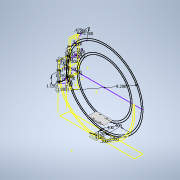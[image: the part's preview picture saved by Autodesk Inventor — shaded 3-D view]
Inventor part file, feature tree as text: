
AUTODESK INVENTOR PART (.ipt)
format: ipt  version: 2022 (Build 260153000, 153)  size: 395,776 bytes
history: native  units: in
note: dims shown in document units (in); Inventor stores cm internally (conversion verified against a paired STEP export)
features: extrude x21, sketch x18, projected_geometry x18, plane x1
ambient origin geometry x8: Origin, YZ Plane, XZ Plane, XY Plane, X Axis, Y Axis, Z Axis, Center Point
bodies: Solid1 (feature_tree)
feature tree (58):
  sketch  "Sketch1"  dims[d0=9.2in d1=0.2in]
  extrude  "Extrusion1"  Depth=0.2in
  extrude  "Extrusion2"  Depth=1.0in TaperAngle=0.0deg
  sketch  "Sketch3"  dims[d6=1.35in d7=0.12in]
  extrude  "Extrusion3"  Depth=0.12in
  extrude  "Extrusion4"  Depth=0.12in
  sketch  "Sketch4"  dims[d8=0.12in d9=0.12in]
  extrude  "Extrusion5"  Depth=1.15in
  extrude  "Extrusion6"  Depth=0.226in
  extrude  "Extrusion7"  Depth=1.0in TaperAngle=0.0deg
  sketch  "Sketch6"  dims[d12=0.1in d13=0.226in]
  plane  "Work Plane1"
  sketch  "Sketch7"  dims[d14=1.0in d15=0.0in d16=1.5in d17=0.0in]
  extrude  "Extrusion8"  Depth=1.5in TaperAngle=0.0deg
  extrude  "Extrusion9"  Depth=1.3in
  extrude  "Extrusion10"  Depth=0.475in
  sketch  "Sketch9"  dims[d22=0.66in d23=1.3in]
  sketch  "Sketch10"  dims[d24=0.26in d25=0.475in]
  extrude  "Extrusion11"  Depth=0.13in
  extrude  "Extrusion12"  Depth=1.0in
  extrude  "Extrusion13"  Depth=0.175in
  extrude  "Extrusion14"  Depth=1.5in TaperAngle=0.0deg
  extrude  "Extrusion15"  Depth=0.12in
  extrude  "Extrusion16"  Depth=0.4in
  extrude  "Extrusion17"  Depth=0.12in
  sketch  "Sketch15"  dims[d35=0.12in d36=0.12in]
  extrude  "Extrusion18"  Depth=1.0in
  sketch  "Sketch16"  dims[d37=0.4in d38=0.4in]
  extrude  "Extrusion19"  Depth=1.0in TaperAngle=0.0deg
  extrude  "Extrusion20"  Depth=1.0in
  extrude  "Extrusion21"  Depth=1.0in
  sketch  "Sketch2"  dims[d2=1.0in d3=0.0in d4=1.0in d5=0.0in]
  projected_geometry  "Projected Loop1"
  projected_geometry  "Projected Loop2"
  projected_geometry  "Projected Loop3"
  sketch  "Sketch5"  dims[d10=0.12in d11=1.15in]
  projected_geometry  "Projected Loop4"
  projected_geometry  "Projected Loop5"
  projected_geometry  "Projected Loop6"
  sketch  "Sketch8"  dims[d18=1.5in d19=0.0in d20=1.5in d21=0.0in]
  projected_geometry  "Projected Loop7"
  projected_geometry  "Projected Loop8"
  projected_geometry  "Projected Loop9"
  projected_geometry  "Projected Loop10"
  sketch  "Sketch11"  dims[d26=0.31in d27=0.13in]
  projected_geometry  "Projected Loop11"
  sketch  "Sketch12"  dims[d28=1.0in d29=0.12in]
  sketch  "Sketch13"  dims[d30=0.12in d31=0.175in]
  projected_geometry  "Projected Loop12"
  projected_geometry  "Projected Loop13"
  projected_geometry  "Projected Loop14"
  projected_geometry  "Projected Loop15"
  projected_geometry  "Projected Loop16"
  sketch  "Sketch14"  dims[d32=0.175in d33=1.5in d34=0.0in]
  projected_geometry  "Projected Loop17"
  projected_geometry  "Projected Loop18"
  sketch  "Sketch17"  dims[d39=0.1in d40=0.12in]
  sketch  "Sketch18"  dims[d41=0.12in d42=0.1in d43=1.5in d44=0.0in d45=1.5in d46=0.2in d47=1.0in d48=0.0in d49=4.0in d50=0.0in d51=0.475in d52=0.26in d53=1.3in d54=0.13in d55=0.31in d56=0.66in d57=0.12in d58=0.1in d59=0.12in d60=0.12in d61=0.12in d62=1.15in d63=3.0in d64=0.0in d65=0.2in d66=0.0in d67=29.0in d68=0.0in d69=0.12in d70=0.175in d71=0.12in d72=0.65in d73=2.0in d74=0.0in d75=2.0in d76=0.0in d77=1.0in d78=0.0in d79=0.8661in d80=0.12in d81=0.12in d82=1.15in d83=0.12in d84=0.12in d85=2.0in d86=0.0in d87=1.0in d88=0.0in d89=1.95in d90=1.95in d91=1.0in d92=0.0in d93=0.0in d94=0.0in d95=0.0in d96=0.0in]
